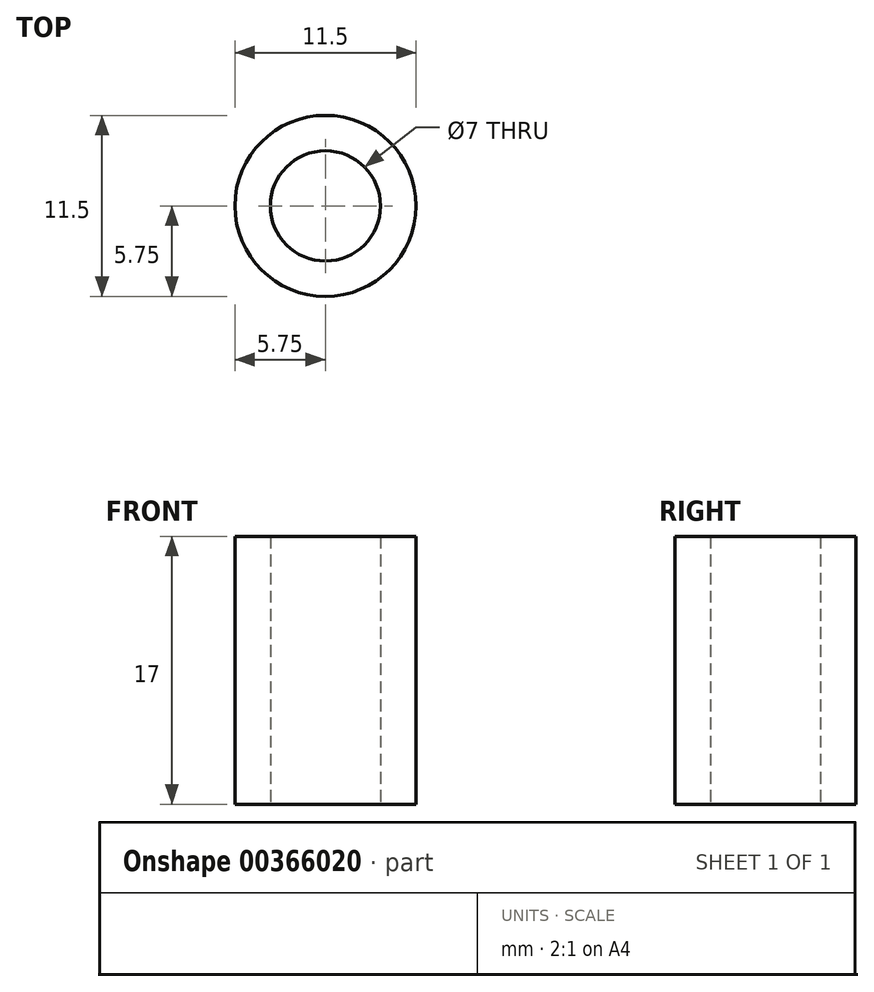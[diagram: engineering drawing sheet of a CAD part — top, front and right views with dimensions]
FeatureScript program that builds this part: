
annotation { "Feature Type Name" : "Feature", "Feature Type Description" : "" }
export const myFeature = defineFeature(function(context is Context, id is Id, definition is map)
    precondition{}
    {
        {
            var Q0;
            Q0=qCreatedBy(makeId("Top.planeOp"),FACE);
            var sketch = newSketch(context, id + "F0", { "sketchPlane" : qUnion([Q0])});
            skCircle(sketch, "E0", {"center": v(0, 0) * mm, "radius": 3.5 * mm});
            skCircle(sketch, "E1", {"center": v(0, 0) * mm, "radius": 5.75 * mm});
            skSolve(sketch);
        }
        {
            var Q0;
            Q0=makeQuery(id+"F0.imprint","IMPRINT",FACE,{"disambiguationData":[TD([[makeQuery(id+"F0.imprint","IMPRINT",EDGE,{"derivedFrom":sQuery(id+"F0.wireOp",EDGE,"E0")}),-1.0]])]});
            extrude(context, id + "F1", {"entities" : qUnion([Q0]), "depth" : 17 * mm});
        }
    });
